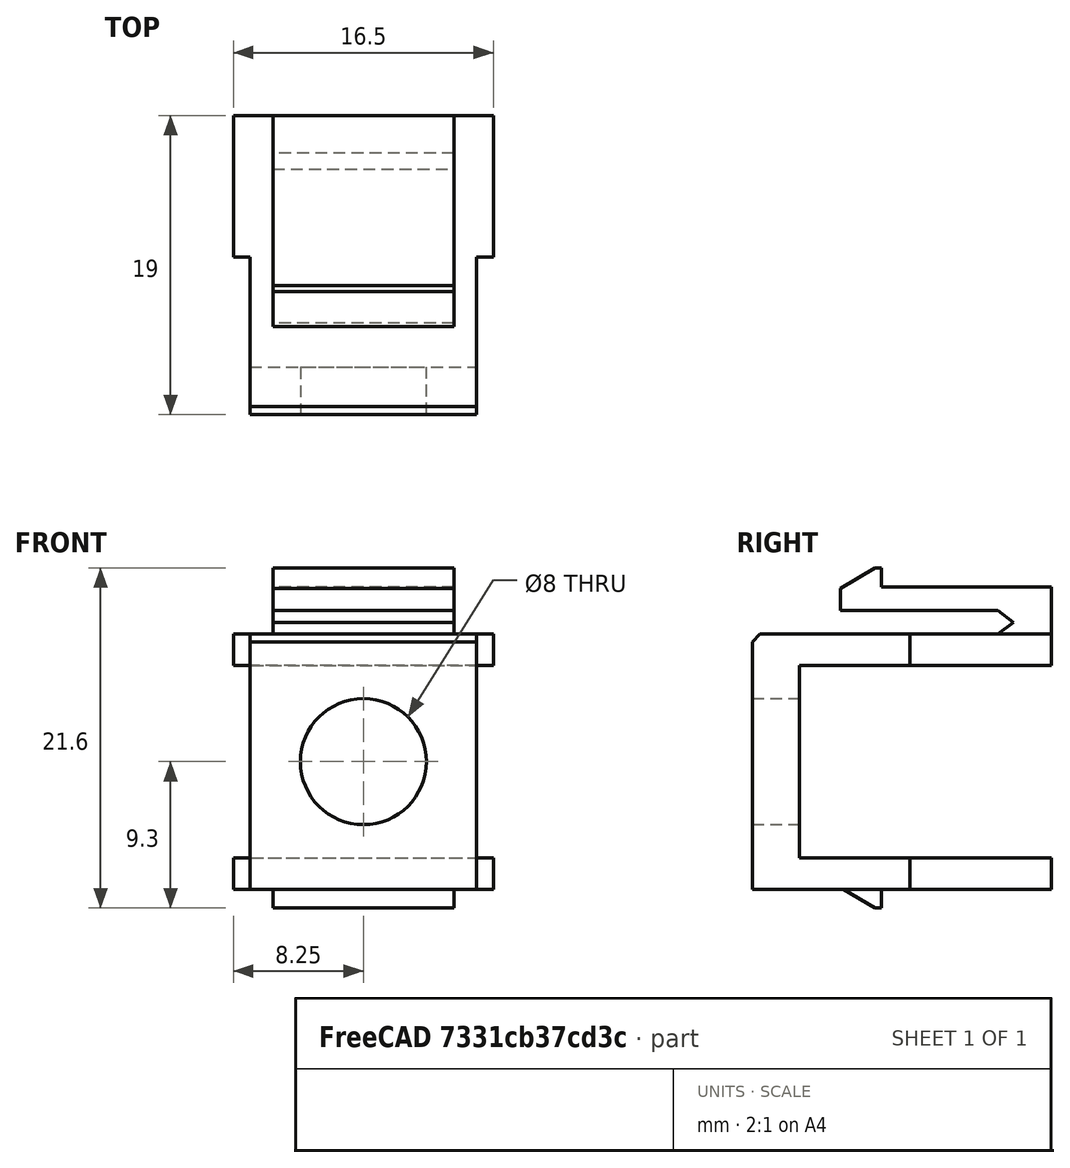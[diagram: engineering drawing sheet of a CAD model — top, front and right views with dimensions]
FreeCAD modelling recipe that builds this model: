
FCSTD DOCUMENT  (FreeCAD 1.0R39319 (Git))
Label: BUTTON-LED_Keystone
License: All rights reserved
LicenseURL: https://en.wikipedia.org/wiki/All_rights_reserved
objects: Sketcher::SketchObject×2, PartDesign::Pocket×2, Part::Feature×1, PartDesign::FeatureBase×1, PartDesign::Body×1, App::Part×1, App::FeaturePython×1, Assembly::JointGroup×1, Assembly::AssemblyObject×1
note: 14 computed .brp shape members not serialized (recipe doc carries the construction recipe); baked Part::Feature solids carry a one-line shape summary decoded from their .brp

FEATURE [Part::Feature] keystone_blank_insert_chamfer002_solid  label="keystone_blank_insert_chamfer002 (Solid)"
  shape: bbox 16.5 x 19 x 21.6 mm, 39 faces (baked)
FEATURE [PartDesign::FeatureBase] BaseFeature
  BaseFeature = -> keystone_blank_insert_chamfer002_solid
  Suppressed = false
FEATURE [Sketcher::SketchObject] Sketch
  ArcFitTolerance = 1e-06
  AttachmentSupport = -> [BaseFeature]
  ExternalGeometry = -> [BaseFeature]
  FullyConstrained = true
  MakeInternals = false
  MapMode = 5
  Placement = pos=(0,0,0) rot=(0.57735,-0.57735,-0.57735;2.0944rad)
  sketch-geometry (3):
    g0: LineSegment StartX=-6 StartY=2 StartZ=0 EndX=-3 EndY=3 EndZ=0
    g1: LineSegment StartX=-3 StartY=3 StartZ=0 EndX=-3 EndY=2 EndZ=0
    g2: LineSegment StartX=-3 StartY=2 StartZ=0 EndX=-6 EndY=2 EndZ=0
  constraints (7):
    c: Coincident(g1,g0)
    c: Vertical(g1)
    c: Coincident(g2,g1)
    c: Coincident(g2,g-3)
    c: Horizontal(g2)
    c: Coincident(g0,g2)
    c: Coincident(g0,g-3)
FEATURE [PartDesign::Pocket] Pocket
  BaseFeature = -> BaseFeature
  Direction = (1,0,0)
  Length = 5
  Length2 = 5
  Midplane = true
  Profile = -> Sketch
  ReferenceAxis = -> Sketch [N_Axis]
  Refine = true
  Suppressed = false
  Type = 1
FEATURE [Sketcher::SketchObject] Sketch001
  ArcFitTolerance = 1e-06
  AttachmentSupport = -> [Pocket]
  ExternalGeometry = -> [Pocket]
  FullyConstrained = true
  MakeInternals = false
  MapMode = 5
  Placement = pos=(0,3,0) rot=(0,0.707107,0.707107;3.14159rad)
  sketch-geometry (3):
    g0: LineSegment [constr] StartX=-14.4 StartY=14.2 StartZ=0 EndX=1e-16 EndY=2 EndZ=0
    g1: GeomPoint [constr] X=-7.2 Y=8.1 Z=0
    g2: Circle CenterX=-7.2 CenterY=8.1 CenterZ=0 NormalX=0 NormalY=0 NormalZ=1 AngleXU=0 Radius=4
  constraints (5):
    c: Coincident(g0,g-3)
    c: Coincident(g0,g-4)
    c: Symmetric(g0,g0,g1)
    c: Diameter(g2) = 8
    c: Coincident(g2,g1)
FEATURE [PartDesign::Pocket] Pocket001
  BaseFeature = -> Pocket
  Direction = (0,-1,2e-16)
  Length = 5
  Length2 = 5
  Profile = -> Sketch001
  ReferenceAxis = -> Sketch001 [N_Axis]
  Refine = true
  Suppressed = false
  Type = 1
FEATURE [PartDesign::Body] Body
  AllowCompound = false
  BaseFeature = -> keystone_blank_insert_chamfer002_solid
  Group = -> [BaseFeature,Sketch,Pocket,Sketch001,Pocket001]
  Origin = -> Origin
  Tip = -> Pocket001
FEATURE [App::Part] Part  label="Keystone"
  Group = -> [keystone_blank_insert_chamfer002_solid,Body]
  Origin = -> Origin001
FEATURE [App::FeaturePython] GroundedJoint  # Assembly grounded joint (typed FeaturePython)
  ObjectToGround = -> Part
FEATURE [Assembly::JointGroup] Joints
  Group = -> [GroundedJoint]
FEATURE [Assembly::AssemblyObject] Assembly  label="BUTTON-LED_Keystone"
  Group = -> [Joints,Part,GroundedJoint]
  Origin = -> Origin004
  Type = Assembly
